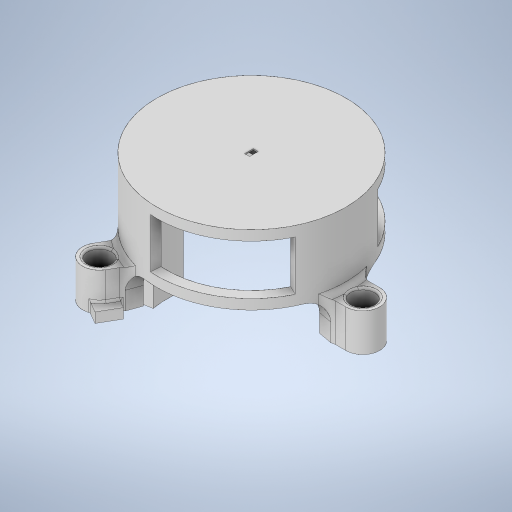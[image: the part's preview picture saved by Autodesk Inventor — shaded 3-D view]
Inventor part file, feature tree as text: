
AUTODESK INVENTOR PART (.ipt)
format: ipt  version: 2024.2 (Build 282272000, 272)  size: 1,166,848 bytes
history: native  units: in
note: dims shown in document units (in); Inventor stores cm internally (conversion verified against a paired STEP export)
features: extrude x12, sketch x12, fillet x8, projected_geometry x5, pattern_circular x1, plane x1
ambient origin geometry x8: Origin, YZ Plane, XZ Plane, XY Plane, X Axis, Y Axis, Z Axis, Center Point
bodies: Solid1 (feature_tree)
feature tree (39):
  extrude  "Extrusion1"  Depth=0.25in TaperAngle=0.0deg
  extrude  "Extrusion2"  Depth=1.1811in TaperAngle=360.0deg
  extrude  "Extrusion3"  Depth=0.25in TaperAngle=0.0deg
  extrude  "Extrusion4"  Depth=0.597in
  fillet  "Fillet1"  Radius=0.95in
  fillet  "Fillet2"  Radius=0.5in
  fillet  "Fillet3"  Radius=0.25in
  pattern_circular  "Circular Pattern1"  Count=3 Angle=360.0deg
  fillet  "Fillet4"  Radius=0.05in
  extrude  "Extrusion6"  Depth=0.125in
  extrude  "Extrusion7"  Depth=0.0625in
  extrude  "Extrusion8"  Depth=0.82in
  extrude  "Extrusion9"  Depth=0.11in
  extrude  "Extrusion10"  Depth=0.25in
  extrude  "Extrusion11"  Depth=0.016in
  extrude  "Extrusion12"  Depth=0.05in
  fillet  "Fillet8"  Radius=0.016in
  plane  "Work Plane1"
  extrude  "Extrusion14"  Depth=0.05in
  fillet  "Fillet9"  Radius=0.031in
  fillet  "Fillet10"  Radius=0.031in
  fillet  "Fillet11"  Radius=0.031in
  sketch  "Sketch1"  dims[d0=4.75in d1=0.25in d2=0.0in]
  sketch  "Sketch2"  dims[d3=0.25in d4=1.1811in d6=360.0deg]
  projected_geometry  "Projected Loop1"
  sketch  "Sketch3"  dims[d8=1.5in d9=0.0in d10=0.25in d11=0.0in]
  projected_geometry  "Projected Loop2"
  sketch  "Sketch4"  dims[d12=0.847in d13=0.597in d14=0.95in d15=0.0in d16=0.5in d17=0.25in]
  projected_geometry  "Projected Loop3"
  sketch  "Sketch6"  dims[d18=0.125in d19=1.1811in d20=360.0deg d24=0.05in]
  sketch  "Sketch7"  dims[d30=0.22in d31=0.125in]
  sketch  "Sketch8"  dims[d32=0.11in d33=0.0625in]
  projected_geometry  "Projected Loop4"
  sketch  "Sketch9"  dims[d34=0.0in d35=0.0in d36=0.82in]
  sketch  "Sketch10"  dims[d37=0.625in d38=0.11in]
  sketch  "Sketch11"  dims[d39=0.25in d40=0.25in]
  projected_geometry  "Projected Loop5"
  sketch  "Sketch12"  dims[d41=0.219in d42=0.0in d43=0.016in]
  sketch  "Sketch14"  dims[d44=0.016in d45=0.016in d46=0.016in d47=0.031in d48=0.031in d49=0.031in d50=0.031in d52=0.031in d53=0.0in d59=0.21in d60=0.1in d61=0.1in d64=0.0625in d65=0.0625in d66=0.06in d67=0.0in d68=0.847in d69=2.5in d70=0.0in d71=0.375in d72=0.625in d74=0.75in d75=0.0in d84=0.3in d85=1.0in d86=0.0in d87=0.05in d88=-0.375in d93=0.25in d95=90.0deg d96=0.5224in d97=0.25in d98=0.0in d99=0.05in d100=0.18in d102=0.3125in d105=0.5in d106=0.05in d107=0.05in d108=0.15in d92=0.5in d94=0.5in]
